# Revit family: Mittenabhängung GMA M6FS,GMA M68FS,GMA M10 FS,GMA M6FT,GMA M8 FT,GMA M10 FT,GMA M6 A4,GMA M8 A4,GMA M10 A4
name_source: partatom
category: Generic Models
revit_build: Autodesk Revit 2017 (Build: 20160225_1515(x64)
units: mm (PartAtom-declared; Revit-internal decimal feet)

## family parameters
Always vertical = Yes
Can host rebar = No
Cut with Voids When Loaded = No
Part Type = Normal
Room Calculation Point = No
Round Connector Dimension = Use Diameter
Shared = No
Work Plane-Based = No

## types (9) — shared parameters
Manufacturer = OBO Bettermann
Type Image = <None>
URL = http://www.obo-bettermann.com
Width = 60 mm  [stored 0.19685 ft]
Width 1 = 40 mm  [stored 0.131234 ft]
Width/2 = 30 mm  [stored 0.0984252 ft]

## per-type parameters (varying)
| type | Diameter | GTIN | Manufacturer Art.No. | Material |
| GMA M6 FS | 7 mm  [stored 0.0229659 ft] | 4012196421695 | 6015220 | Strip-galvanised |
| GMA M6 FT | 7 mm  [stored 0.0229659 ft] | 4012195649786 | 6015224 | Hot-dip galvanised |
| GMA M6 A4 | 7 mm  [stored 0.0229659 ft] | 4012195928720 | 6015228 | Stainless steel, A4 |
| GMA M8 FS | 9 mm  [stored 0.0295276 ft] | 4012196421572 | 6015239 | Strip-galvanised |
| GMA M10 FT | 11 mm  [stored 0.0360892 ft] | 4012196942619 | 6015255 | Hot-dip galvanised |
| GMA M10 A4 | 11 mm  [stored 0.0360892 ft] | 4012196942671 | 6015261 | Stainless steel, A4 |
| GMA M8 FT | 9 mm  [stored 0.0295276 ft] | 4012195928737 | 6015243 | Hot-dip galvanised |
| GMA M8 A4 | 9 mm  [stored 0.0295276 ft] | 4012195928744 | 6015245 | Stainless steel, A4 |
| GMA M10 FS | 11 mm  [stored 0.0360892 ft] | 4012196421510 | 6015247 | Strip-galvanised |

note: column(s) folded — value = type name in every type: Article Type

note: [stored X ft] marks values corroborated as IEEE doubles in the binary element streams (Revit-internal decimal feet)

## geometry (parser evidence)
native form markers: Sweep x2
no freeform markers — native parametric forms only
